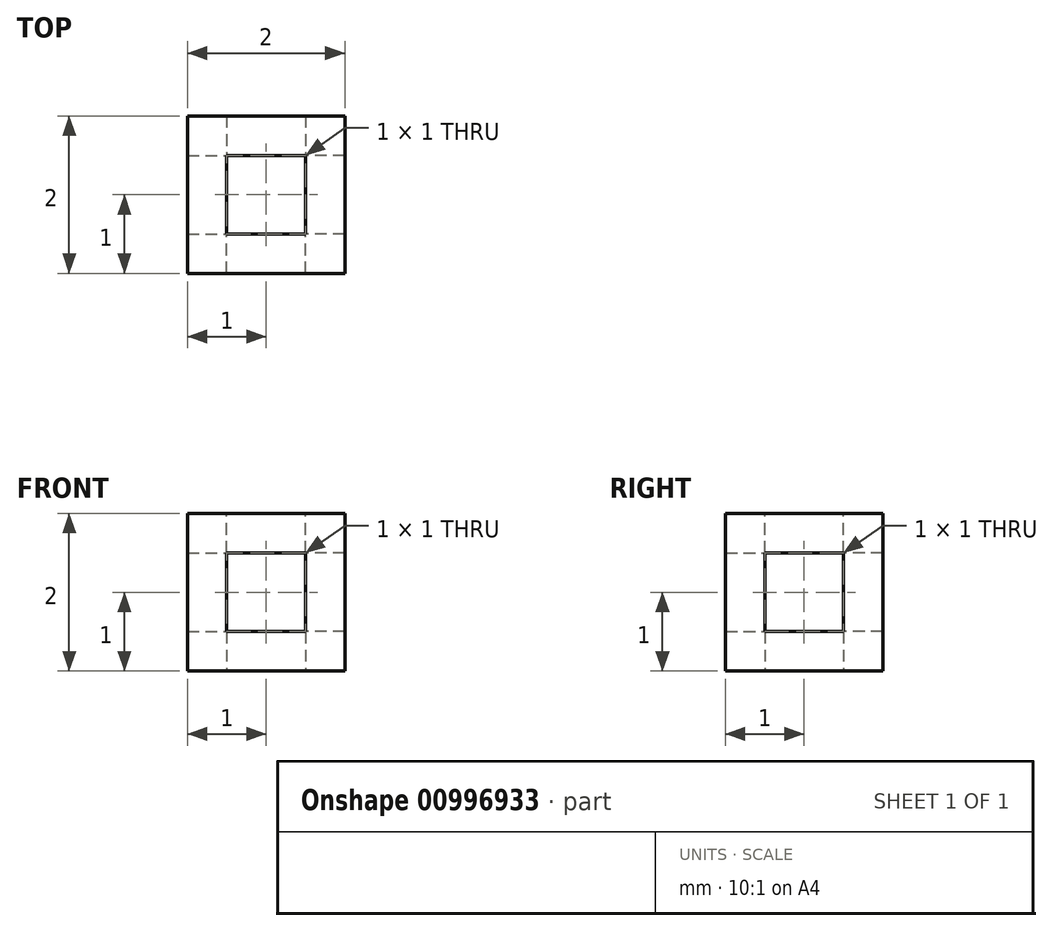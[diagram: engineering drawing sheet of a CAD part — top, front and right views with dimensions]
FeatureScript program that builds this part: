
annotation { "Feature Type Name" : "Feature", "Feature Type Description" : "" }
export const myFeature = defineFeature(function(context is Context, id is Id, definition is map)
    precondition{}
    {
        {
            var Q0;
            Q0=qCreatedBy(makeId("Top.planeOp"),FACE);
            var sketch = newSketch(context, id + "F0", { "sketchPlane" : qUnion([Q0])});
            skLineSegment(sketch, "E0.bottom", {"start": v(0, 0) * mm, "end": v(2, 0) * mm});
            skLineSegment(sketch, "E0.top", {"start": v(0, 2) * mm, "end": v(2, 2) * mm});
            skLineSegment(sketch, "E0.left", {"start": v(0, 0) * mm, "end": v(0, 2) * mm});
            skLineSegment(sketch, "E0.right", {"start": v(2, 0) * mm, "end": v(2, 2) * mm});
            skLineSegment(sketch, "E1.bottom", {"start": v(0.5, 0.5) * mm, "end": v(1.5, 0.5) * mm});
            skLineSegment(sketch, "E1.top", {"start": v(0.5, 1.5) * mm, "end": v(1.5, 1.5) * mm});
            skLineSegment(sketch, "E1.left", {"start": v(0.5, 0.5) * mm, "end": v(0.5, 1.5) * mm});
            skLineSegment(sketch, "E1.right", {"start": v(1.5, 0.5) * mm, "end": v(1.5, 1.5) * mm});
            skLineSegment(sketch, "E2", {"start": v(1, 2) * mm, "end": v(1, 1.5) * mm, "construction": true});
            skPoint(sketch, "E2.endSnap0", {"position": v(1, 1.5) * mm});
            skLineSegment(sketch, "E3", {"start": v(0.5, 1) * mm, "end": v(0, 1) * mm, "construction": true});
            skSolve(sketch);
        }
        {
            var Q0;
            Q0=makeQuery(id+"F0.imprint","IMPRINT",FACE,{"disambiguationData":[TD([[makeQuery(id+"F0.imprint","IMPRINT",EDGE,{"derivedFrom":sQuery(id+"F0.wireOp",EDGE,"E0.bottom")}),1.0]])]});
            extrude(context, id + "F1", {"entities" : qUnion([Q0]), "depth" : 0.5 * mm, "offsetDistance" : 25 * mm});
        }
        {
            var Q0;
            Q0=makeQuery(id+"F1.opExtrude","CAP_FACE",FACE,{"disambiguationData":[OSD([sQuery(id+"F0.wireOp",EDGE,"E0.bottom"),sQuery(id+"F0.wireOp",EDGE,"E0.top"),sQuery(id+"F0.wireOp",EDGE,"E0.left"),sQuery(id+"F0.wireOp",EDGE,"E0.right"),sQuery(id+"F0.wireOp",EDGE,"E1.bottom"),sQuery(id+"F0.wireOp",EDGE,"E1.top"),sQuery(id+"F0.wireOp",EDGE,"E1.left"),sQuery(id+"F0.wireOp",EDGE,"E1.right")])],"isStart":false});
            var sketch = newSketch(context, id + "F2", { "sketchPlane" : qUnion([Q0])});
            skLineSegment(sketch, "E4.bottom", {"start": v(0, 0) * mm, "end": v(0.5, 0) * mm});
            skLineSegment(sketch, "E4.top", {"start": v(0, 0.5) * mm, "end": v(0.5, 0.5) * mm});
            skLineSegment(sketch, "E4.left", {"start": v(0, 0) * mm, "end": v(0, 0.5) * mm});
            skLineSegment(sketch, "E4.right", {"start": v(0.5, 0) * mm, "end": v(0.5, 0.5) * mm});
            skLineSegment(sketch, "E5.bottom", {"start": v(0, 2) * mm, "end": v(0.5, 2) * mm});
            skLineSegment(sketch, "E5.top", {"start": v(0, 1.5) * mm, "end": v(0.5, 1.5) * mm});
            skLineSegment(sketch, "E5.left", {"start": v(0, 2) * mm, "end": v(0, 1.5) * mm});
            skLineSegment(sketch, "E5.right", {"start": v(0.5, 2) * mm, "end": v(0.5, 1.5) * mm});
            skLineSegment(sketch, "E6.bottom", {"start": v(2, 2) * mm, "end": v(1.5, 2) * mm});
            skLineSegment(sketch, "E6.top", {"start": v(2, 1.5) * mm, "end": v(1.5, 1.5) * mm});
            skLineSegment(sketch, "E6.left", {"start": v(2, 2) * mm, "end": v(2, 1.5) * mm});
            skLineSegment(sketch, "E6.right", {"start": v(1.5, 2) * mm, "end": v(1.5, 1.5) * mm});
            skLineSegment(sketch, "E7.bottom", {"start": v(2, 0) * mm, "end": v(1.5, 0) * mm});
            skLineSegment(sketch, "E7.top", {"start": v(2, 0.5) * mm, "end": v(1.5, 0.5) * mm});
            skLineSegment(sketch, "E7.left", {"start": v(2, 0) * mm, "end": v(2, 0.5) * mm});
            skLineSegment(sketch, "E7.right", {"start": v(1.5, 0) * mm, "end": v(1.5, 0.5) * mm});
            skSolve(sketch);
        }
        {
            var Q0;
            Q0=makeQuery(id+"F2.imprint","IMPRINT",FACE,{"disambiguationData":[TD([[makeQuery(id+"F2.imprint","IMPRINT",EDGE,{"derivedFrom":sQuery(id+"F2.wireOp",EDGE,"E5.bottom")}),-1.0]])]});
            var Q1;
            Q1=makeQuery(id+"F2.imprint","IMPRINT",FACE,{"disambiguationData":[TD([[makeQuery(id+"F2.imprint","IMPRINT",EDGE,{"derivedFrom":sQuery(id+"F2.wireOp",EDGE,"E4.bottom")}),1.0]])]});
            var Q2;
            Q2=makeQuery(id+"F2.imprint","IMPRINT",FACE,{"disambiguationData":[TD([[makeQuery(id+"F2.imprint","IMPRINT",EDGE,{"derivedFrom":sQuery(id+"F2.wireOp",EDGE,"E7.bottom")}),1.0]])]});
            var Q3;
            Q3=makeQuery(id+"F2.imprint","IMPRINT",FACE,{"disambiguationData":[TD([[makeQuery(id+"F2.imprint","IMPRINT",EDGE,{"derivedFrom":sQuery(id+"F2.wireOp",EDGE,"E6.bottom")}),-1.0]])]});
            extrude(context, id + "F3", {"entities" : qUnion([Q0, Q1, Q2, Q3]), "operationType" : NewBodyOperationType.ADD, "depth" : 0.5 * mm, "offsetDistance" : 25 * mm});
        }
        {
            var Q0;
            Q0=makeQuery(id+"F1.opExtrude","SWEPT_BODY",BODY,{"disambiguationData":[OSD([sQuery(id+"F0.wireOp",EDGE,"E0.bottom"),sQuery(id+"F0.wireOp",EDGE,"E0.top"),sQuery(id+"F0.wireOp",EDGE,"E0.left"),sQuery(id+"F0.wireOp",EDGE,"E0.right"),sQuery(id+"F0.wireOp",EDGE,"E1.bottom"),sQuery(id+"F0.wireOp",EDGE,"E1.top"),sQuery(id+"F0.wireOp",EDGE,"E1.left"),sQuery(id+"F0.wireOp",EDGE,"E1.right")])]});
            var Q1;
            Q1=makeQuery(id+"F3.opExtrude","CAP_FACE",FACE,{"disambiguationData":[OSD([sQuery(id+"F2.wireOp",EDGE,"E4.bottom"),sQuery(id+"F2.wireOp",EDGE,"E4.top"),sQuery(id+"F2.wireOp",EDGE,"E4.left"),sQuery(id+"F2.wireOp",EDGE,"E4.right")])],"isStart":false});
            mirror(context, id + "F4", {"operationType" : NewBodyOperationType.ADD, "entities" : qUnion([Q0]), "mirrorPlane" : qUnion([Q1])});
        }
    });
